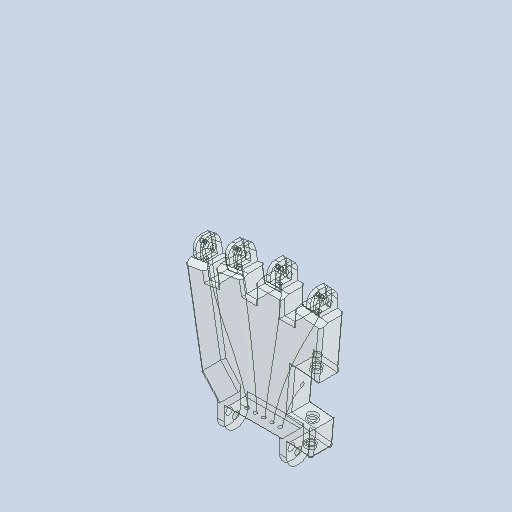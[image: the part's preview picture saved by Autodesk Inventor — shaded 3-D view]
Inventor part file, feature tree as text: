
AUTODESK INVENTOR PART (.ipt)
format: ipt  version: 2022 (Build 260153000, 153)  size: 836,608 bytes
history: native  units: in
note: dims shown in document units (in); Inventor stores cm internally (conversion verified against a paired STEP export)
features: sketch x38, extrude x20, fillet x15, chamfer x12, hole x7, plane x6, sweep x5, thread x3
ambient origin geometry x8: Origin, YZ Plane, XZ Plane, XY Plane, X Axis, Y Axis, Z Axis, Center Point
bodies: Solid1 (feature_tree)
feature tree (106):
  extrude  "Extrusion1"  Depth=0.689in
  chamfer  "Chamfer1"  Distance=0.6693in
  chamfer  "Chamfer2"  Distance=0.0787in Angle=45.0deg
  chamfer  "Chamfer3"  Distance=0.0787in Angle=45.0deg
  chamfer  "Chamfer4"  Distance=0.0787in Angle=45.0deg
  extrude  "Extrusion2"  Depth=0.0787in
  fillet  "Fillet1"  Radius=0.1378in
  fillet  "Fillet2"  Radius=0.0787in
  fillet  "Fillet3"  Radius=0.0591in
  hole  "Hole2"  [1 undecoded]
  extrude  "Extrusion3"  Depth=0.3937in
  fillet  "Fillet4"  Radius=0.2953in
  fillet  "Fillet5"  Radius=0.1772in
  fillet  "Fillet6"  Radius=0.3543in
  hole  "Hole3"  [1 undecoded]
  extrude  "Extrusion4"  Depth=0.2362in
  fillet  "Fillet7"  Radius=0.4724in
  fillet  "Fillet8"  Radius=0.0787in
  fillet  "Fillet9"  Radius=0.2362in
  hole  "Hole4"  [1 undecoded]
  extrude  "Extrusion5"  Depth=0.0787in
  fillet  "Fillet10"  Radius=0.3543in
  fillet  "Fillet11"  Radius=0.1083in
  fillet  "Fillet12"  Radius=0.1378in
  hole  "Hole5"  [1 undecoded]
  hole  "Hole6"  [1 undecoded]
  hole  "Hole7"  [1 undecoded]
  extrude  "Extrusion6"  Depth=0.0787in
  extrude  "Extrusion7"  Depth=0.0787in
  hole  "Hole8"  [1 undecoded]
  extrude  "Extrusion8"  Depth=0.4724in TaperAngle=0.0deg
  plane  "Work Plane6"
  sketch  "Sketch27"  dims[d25=0.2953in]
  plane  "Work Plane5"
  sketch  "Sketch28"  dims[d26=0.6871in]
  plane  "Work Plane4"
  sketch  "Sketch29"  dims[d31=0.5906in]
  plane  "Work Plane3"
  sketch  "Sketch30"  dims[d32=2.5591in]
  plane  "Work Plane1"
  sketch  "Sketch31"  dims[d33=0.5497in d34=0.6693in d35=0.0in d36=0.0787in d37=0.1969in d38=45.0deg d39=0.0787in d40=0.1969in d41=45.0deg d42=0.0787in d43=0.1969in d44=45.0deg]
  sketch  "Sketch32"  dims[d45=0.0787in d46=0.1969in d47=45.0deg d50=0.1083in d51=0.1378in d52=0.0787in d53=0.0591in]
  sketch  "Sketch33"  dims[d54=0.4724in d55=0.0in d56=0.2362in]
  sketch  "Sketch34"  dims[d57=0.0787in d58=0.3937in d67=0.2953in]
  sketch  "Sketch35"  dims[d68=0.1575in d69=0.2362in d70=0.1575in d71=0.0787in d72=90.0deg d73=0.315in d74=0.8108in d75=0.1772in d76=0.3543in]
  sketch  "Sketch36"  dims[d77=0.1083in d78=0.1378in]
  sweep  "Sweep1"
  sweep  "Sweep2"
  sweep  "Sweep3"
  sweep  "Sweep4"
  plane  "Work Plane2"
  sweep  "Sweep5"
  fillet  "Fillet13"  Radius=0.2756in
  extrude  "Extrusion10"  Depth=0.0492in TaperAngle=0.0deg
  extrude  "Extrusion11"  Depth=0.3937in
  extrude  "Extrusion12"  Depth=0.0787in TaperAngle=0.0deg
  fillet  "Fillet14"  Radius=0.0984in
  extrude  "Extrusion13"  Depth=0.0492in
  fillet  "Fillet15"  Radius=0.0984in
  extrude  "Extrusion14"  Depth=0.0492in
  chamfer  "Chamfer5"  Distance=0.0984in
  extrude  "Extrusion15"  TaperAngle=0.0deg  [1 undecoded]
  chamfer  "Chamfer6"  [1 undecoded]
  extrude  "Extrusion16"  TaperAngle=0.0deg  [1 undecoded]
  chamfer  "Chamfer7"  [1 undecoded]
  extrude  "Extrusion17"  TaperAngle=0.0deg  [1 undecoded]
  chamfer  "Chamfer8"  Distance=0.0787in
  extrude  "Extrusion18"  Depth=0.0492in
  chamfer  "Chamfer9"  Distance=0.0984in
  extrude  "Extrusion19"  Depth=0.0492in
  chamfer  "Chamfer10"  Distance=0.0984in
  extrude  "Extrusion20"  Depth=0.0492in TaperAngle=0.0deg
  chamfer  "Chamfer11"  Distance=0.0787in
  extrude  "Extrusion21"  Depth=0.0787in TaperAngle=0.0deg
  chamfer  "Chamfer12"  Distance=0.3346in
  thread  "Thread3"  [1 undecoded]
  thread  "Thread4"  [1 undecoded]
  thread  "Thread5"  [1 undecoded]
  sketch  "Sketch2"  dims[d3=1.9685in d4=0.689in]
  sketch  "Sketch3"  dims[d5=1.2025in]
  sketch  "Sketch5"  dims[d6=0.7874in]
  sketch  "Sketch6"  dims[d7=1.1811in]
  sketch  "Sketch8"  dims[d8=1.4961in]
  sketch  "Sketch9"  dims[d9=0.7874in]
  sketch  "Sketch10"  dims[d12=0.2953in]
  sketch  "Sketch11"  dims[d13=180.0deg]
  sketch  "Sketch12"  dims[d15=0.4724in]
  sketch  "Sketch13"  dims[d16=0.7874in]
  sketch  "Sketch14"  dims[d17=0.2953in]
  sketch  "Sketch15"  dims[d18=0.4134in]
  sketch  "Sketch16"  dims[d19=0.6871in]
  sketch  "Sketch17"  dims[d20=0.7874in]
  sketch  "Sketch18"  dims[d21=0.2953in]
  sketch  "Sketch37"  dims[d79=0.0787in d80=0.0591in d81=0.4724in d82=0.0in d83=0.0787in d84=0.2362in]
  sketch  "Sketch38"  dims[d85=0.3937in d86=0.2953in]
  sketch  "Sketch39"  dims[d87=0.1575in d88=0.2362in d89=0.1575in d90=0.0787in d91=90.0deg d92=0.4998in d93=0.8108in d94=0.1772in d95=0.3543in d96=0.1083in d97=0.1378in]
  sketch  "Sketch40"  dims[d98=0.0591in d99=0.0787in]
  sketch  "Sketch41"  dims[d100=0.4724in d101=0.0in d102=0.2362in]
  sketch  "Sketch43"  dims[d103=0.0787in d104=0.3937in]
  sketch  "Sketch44"  dims[d105=0.2953in]
  sketch  "Sketch45"  dims[d106=0.1575in d107=0.2362in d108=0.1575in d109=0.0787in d110=90.0deg d111=0.4998in d112=0.8108in d113=0.1378in]
  sketch  "Sketch46"  dims[d114=0.2756in d115=0.0787in]
  sketch  "Sketch47"  dims[d116=0.1181in d117=0.0787in]
  sketch  "Sketch48"  dims[d118=0.0591in d119=0.4724in d120=0.0in]
  sketch  "Sketch49"  dims[d121=0.2362in d122=0.0787in]
  sketch  "Sketch50"  dims[d123=0.3937in d124=0.2953in d125=0.1575in d126=0.2362in d127=0.1575in d128=0.0787in d129=90.0deg d130=0.4998in d131=0.8108in d132=0.1969in d133=0.2362in d134=0.119in d135=0.0787in d136=0.5635in d137=0.3937in d138=0.0in d139=0.1969in d140=0.2362in d141=0.1575in d142=0.0787in d143=90.0deg d144=1.2687in d145=0.0in d149=0.2756in d150=0.0787in d151=0.0in d152=0.2756in d153=0.2756in d154=0.6693in d155=0.0in d156=0.1969in d157=0.2362in d158=0.1575in d159=0.0787in d160=90.0deg d161=1.969in d162=0.0in d165=0.3937in d166=0.0787in d167=0.0in d194=0.0984in d195=0.0984in d196=0.0984in d197=0.0984in d198=0.0984in d199=0.0in d200=0.0in d201=0.0in d202=0.0in d203=0.0in d204=0.0in d205=0.0in d206=0.0in d207=0.0in d208=0.0in d209=0.0787in d210=0.2756in d211=0.0984in d212=0.0in d213=0.2756in d214=0.0984in d215=0.0in d218=0.6693in d219=0.0in d220=0.0787in d221=0.0787in d222=0.0in d223=0.3346in d226=0.0689in d227=0.0in d228=0.0098in d229=0.0492in d230=45.0deg d231=0.0689in d232=0.0in d233=0.0098in d234=0.0492in d235=45.0deg d238=0.0689in d239=0.0in d240=0.0098in d241=0.0492in d242=45.0deg d243=0.0689in d244=0.0in d245=0.0098in d246=0.0492in d247=45.0deg d250=0.0689in d251=0.0in d252=0.0098in d253=0.0492in d254=45.0deg d255=0.0689in d256=0.0in d257=0.0098in d258=0.0492in d259=45.0deg d262=0.0591in d263=0.0in d264=0.0098in d265=0.0492in d266=45.0deg d267=0.0591in d268=0.0in d269=0.0098in d270=0.0492in d271=45.0deg d272=0.2953in d273=0.0in d274=0.2953in d275=0.0in d276=0.2953in d277=0.0in d59=0.0in d60=0.0in d61=0.0in d146=0.0295in d147=0.8108in d148=0.0025in d169=0.0394in d170=0.0394in d171=0.0394in d172=0.0059in d173=0.0098in d174=0.0148in d175=0.5635in d176=0.0295in d177=0.8108in d178=0.0025in d179=0.0295in d180=0.0148in d181=0.0344in d182=0.0394in d183=0.0394in d184=0.0394in d185=0.0059in d186=0.0098in d187=0.0148in d188=0.5635in d189=0.0295in d190=0.8108in d191=0.0025in d192=0.0295in d193=0.0148in]
note: 15 required parameter values undecoded (feature->parameter linkage not recoverable at this tier; creation-order binding heuristic only, values carry confidence <= 0.55)
